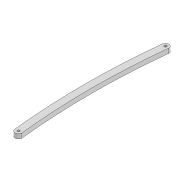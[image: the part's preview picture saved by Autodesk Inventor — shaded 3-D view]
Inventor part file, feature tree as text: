
AUTODESK INVENTOR PART (.ipt)
format: ipt  version: 2022 (Build 260153000, 153)  size: 93,184 bytes
history: native  units: mm
features: extrude x1, sketch x1
ambient origin geometry x8: Origin, YZ Plane, XZ Plane, XY Plane, X Axis, Y Axis, Z Axis, Center Point
bodies: Solid1 (feature_tree)
feature tree (2):
  extrude  "Extrusion1"  Depth=600.0mm
  sketch  "Sketch1"  dims[d0=2.2mm d1=2.2mm d2=6.0mm d3=128.523mm d6=4.0mm d7=0.0mm d14=600.0mm d15=600.0mm]
